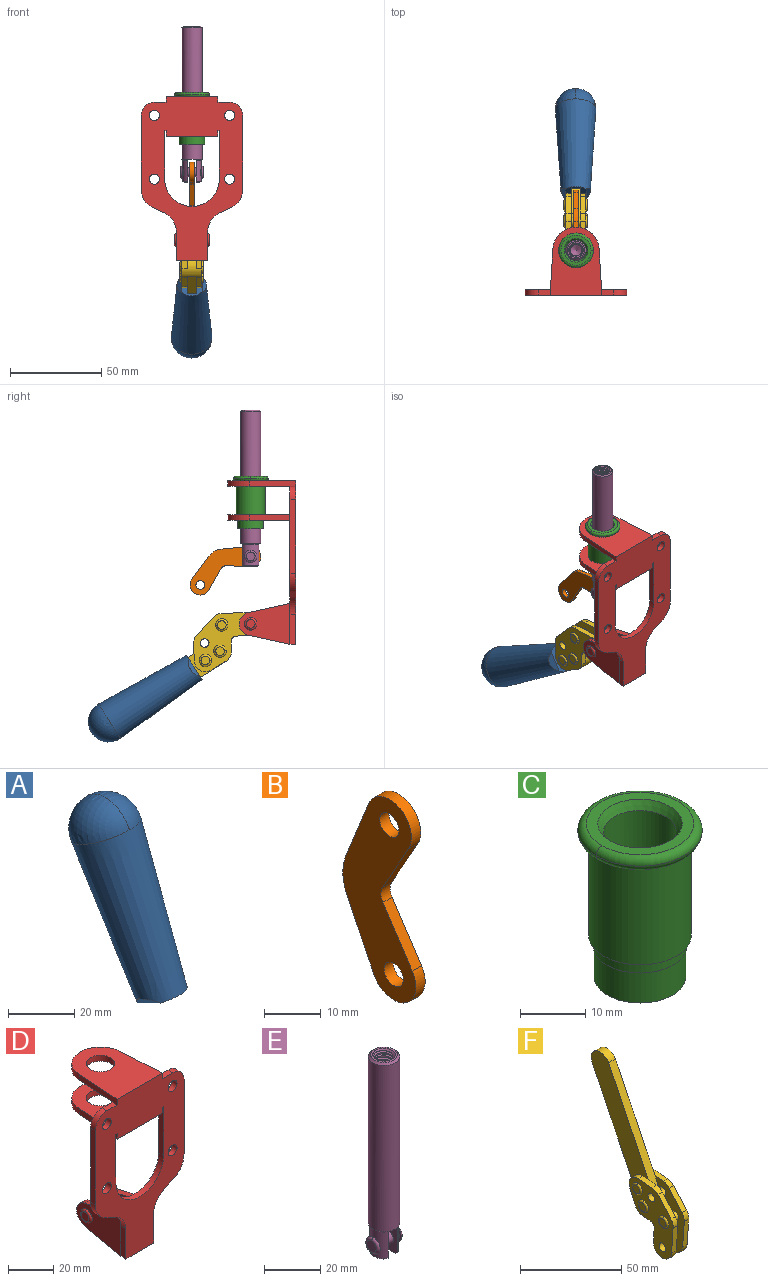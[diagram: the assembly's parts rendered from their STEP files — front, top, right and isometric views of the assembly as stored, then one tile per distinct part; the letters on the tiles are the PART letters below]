
ASSEMBLY  parts=6 mates=5
PART A: 11 faces, bbox 22.3x42.6x64.5 mm
  f0: sphere r=11.13mm, area 411.4mm2, adj f1,f8
  f1: cone r=11.11mm half-angle=3.3deg, axis (0,0.44,0.9), area 3251.8mm2, adj f0,f7,f8,f9,f10
  f2: cylinder r=6.16mm len=11.7mm, axis (1,0,0), area 89.5mm2, adj f3,f4,f5,f6
  f3: plane 60.23x36.75mm, normal (-1,0,0), area 763.6mm2, adj f2,f4,f6,f10
  f4: plane 51.37x25.05mm, normal (0,0.9,-0.44), area 264.2mm2, adj f2,f3,f5,f10
  f5: plane 60.23x36.75mm, normal (1,0,0), area 763.6mm2, adj f2,f4,f6,f10
  f6: plane 51.37x25.05mm, normal (0,-0.9,0.44), area 264.2mm2, adj f2,f3,f5,f10
  f7: plane 9.95x5.95mm, normal (0.71,-0.31,-0.64), area 25.8mm2, adj f1,f10
  f8: sphere r=11.13mm, area 411.4mm2, adj f0,f1
  f9: plane 9.95x5.95mm, normal (-0.71,-0.31,-0.64), area 25.8mm2, adj f1,f10
  f10: plane 14.27x11.38mm, normal (0,-0.44,-0.9), area 106.7mm2, adj f1,f3,f4,f5,f6,f7,f9
PART B: 12 faces, bbox 2.3x18.2x42.8 mm
  f0: cylinder r=2.4mm len=4.8mm, axis (1,0,0), area 34.9mm2, adj f4,f11
  f1: cylinder r=10.41mm len=8.47mm, axis (1,0,0), area 20.2mm2, adj f4,f9,f10,f11
  f2: cylinder r=3.05mm len=3.16mm, axis (1,0,0), area 7.7mm2, adj f4,f6,f7,f11
  f3: cylinder r=2.4mm len=4.8mm, axis (1,0,0), area 34.9mm2, adj f4,f11
  f4: plane 42.81x18.23mm, normal (-1,0,0), area 414.1mm2, adj f0,f1,f2,f3,f5,f6,f7,f8
  f5: cylinder r=5.54mm len=10.67mm, axis (1,0,0), area 41.8mm2, adj f4,f6,f10,f11
  f6: plane 11.66x6.53mm, normal (0,-0.87,-0.49), area 30.9mm2, adj f2,f4,f5,f11
  f7: plane 11.17x7.33mm, normal (0,-0.84,0.55), area 30.9mm2, adj f2,f4,f8,f11
  f8: cylinder r=5.54mm len=10.51mm, axis (1,0,0), area 41.8mm2, adj f4,f7,f9,f11
  f9: plane 13.67x6.67mm, normal (0,0.9,-0.44), area 35.1mm2, adj f1,f4,f8,f11
  f10: plane 14.1x5.7mm, normal (0,0.93,0.37), area 35.1mm2, adj f1,f4,f5,f11
  f11: plane 42.81x18.23mm, normal (1,0,0), area 414.1mm2, adj f0,f1,f2,f3,f5,f6,f7,f8
PART C: 15 faces, bbox 20.6x20.6x28.7 mm
  f0: torus R=8.26mm, axis (0,0,1), area 56.8mm2, adj f1,f10,f12
  f1: torus R=8.26mm, axis (0,0,1), area 56.8mm2, adj f0,f6,f13
  f2: cylinder r=5.59mm len=25.91mm, axis (0,0,1), area 909.6mm2, adj f3,f4
  f3: cone r=6.86mm half-angle=45deg, axis (0,0,-1), area 70.2mm2, adj f2,f14
  f4: cone r=6.47mm half-angle=30deg, axis (0,0,1), area 66.7mm2, adj f2,f13
  f5: cylinder r=7.04mm len=14.07mm, axis (0,0,1), area 252.6mm2, adj f11,f14
  f6: torus R=8.26mm, axis (0,0,1), area 56.8mm2, adj f1,f12,f13
  f7: cylinder r=7.16mm len=14.33mm, axis (0,0,1), area 91.5mm2, adj f9,f11
  f8: cylinder r=7.86mm len=18.42mm, axis (0,0,1), area 909.6mm2, adj f9,f10
  f9: plane 15.72x15.72mm, normal (0,0,-1), area 33mm2, adj f7,f8
  f10: plane 16.51x16.51mm, normal (0,0,-1), area 19.9mm2, adj f0,f8,f12
  f11: plane 14.33x14.33mm, normal (0,0,-1), area 5.7mm2, adj f5,f7
  f12: torus R=8.26mm, axis (0,0,1), area 56.8mm2, adj f0,f6,f10
  f13: plane 16.51x16.51mm, normal (0,0,1), area 82.7mm2, adj f1,f4,f6
  f14: plane 14.07x14.07mm, normal (0,0,-1), area 7.8mm2, adj f3,f5
PART D: 55 faces, bbox 55.7x37.4x89.8 mm
  f0: torus R=2.41mm, axis (-1,0,0), area 15mm2, adj f11,f15,f25
  f1: torus R=2.41mm, axis (-1,0,0), area 15mm2, adj f10,f12,f22
  f2: cylinder r=2.78mm len=5.56mm, axis (0,-1,0), area 54.2mm2, adj f30,f54
  f3: cylinder r=14.99mm len=29.97mm, axis (0,-1,0), area 145.9mm2, adj f30,f49,f53,f54
  f4: cylinder r=2.78mm len=5.56mm, axis (0,-1,0), area 54.2mm2, adj f30,f54
  f5: cylinder r=2.78mm len=5.56mm, axis (0,-1,0), area 54.2mm2, adj f30,f54
  f6: cylinder r=2.78mm len=5.56mm, axis (0,-1,0), area 54.2mm2, adj f30,f54
  f7: cylinder r=6.35mm len=12.7mm, axis (0,0,1), area 123.6mm2, adj f27,f51
  f8: cylinder r=6.35mm len=12.7mm, axis (0,0,-1), area 124.7mm2, adj f21,f35
  f9: cylinder r=2.41mm len=11.18mm, axis (-1,0,0), area 169.4mm2, adj f16,f19
  f10: plane 4.83x4.83mm, normal (1,0,0), area 18.3mm2, adj f1,f12
  f11: plane 4.83x4.83mm, normal (-1,0,0), area 18.3mm2, adj f0,f15
  f12: torus R=2.41mm, axis (-1,0,0), area 15mm2, adj f1,f10,f22
  f13: cylinder r=6.35mm len=12.41mm, axis (1,0,0), area 53.4mm2, adj f18,f19,f22,f23
  f14: cylinder r=6.35mm len=12.41mm, axis (-1,0,0), area 53.4mm2, adj f16,f17,f24,f25
  f15: torus R=2.41mm, axis (-1,0,0), area 15mm2, adj f0,f11,f25
  f16: plane 27.86x22.35mm, normal (1,0,0), area 425.4mm2, adj f9,f14,f17,f24,f30
  f17: plane 22.86x4.97mm, normal (0,0.21,0.98), area 72.5mm2, adj f14,f16,f25,f30
  f18: plane 22.86x4.97mm, normal (0,0.21,0.98), area 72.5mm2, adj f13,f19,f22,f30
  f19: plane 27.86x22.35mm, normal (-1,0,0), area 425.4mm2, adj f9,f13,f18,f23,f30
  f20: cylinder r=12.7mm len=25.35mm, axis (0,0,-1), area 119.8mm2, adj f21,f34,f35,f36
  f21: plane 34.21x28.07mm, normal (0,0,-1), area 702.4mm2, adj f8,f20,f30,f34,f36
  f22: plane 27.96x22.45mm, normal (1,0,0), area 407.2mm2, adj f1,f12,f13,f18,f23,f30,f42,f43
  f23: plane 22.86x4.97mm, normal (0,0.21,-0.98), area 72.5mm2, adj f13,f19,f22,f44
  f24: plane 22.86x4.97mm, normal (0,0.21,-0.98), area 72.5mm2, adj f14,f16,f25,f44
  f25: plane 27.86x22.35mm, normal (-1,0,0), area 407.1mm2, adj f0,f14,f15,f17,f24,f30,f45,f46
  f26: plane 3.1x0.95mm, normal (0,0,-1), area 2.7mm2, adj f30,f49,f50,f54
  f27: plane 34.21x28.07mm, normal (0,0,1), area 702.4mm2, adj f7,f28,f30,f50,f52
  f28: cylinder r=12.7mm len=25.35mm, axis (0,0,1), area 118.8mm2, adj f27,f50,f51,f52
  f29: plane 3.1x0.95mm, normal (0,0,-1), area 2.7mm2, adj f30,f52,f53,f54
  f30: plane 86.54x55.63mm, normal (0,1,0), area 2362.9mm2, adj f2,f3,f4,f5,f6,f16,f17,f18
  f31: plane 40.56x3.1mm, normal (-1,0,0), area 125.7mm2, adj f30,f32,f48,f54
  f32: cylinder r=7.11mm len=7.11mm, axis (0,-1,0), area 34.6mm2, adj f30,f31,f33,f54
  f33: plane 6.67x3.1mm, normal (0,0,1), area 20.4mm2, adj f30,f32,f34,f54
  f34: plane 25.39x3.13mm, normal (-1,0.06,0), area 79.5mm2, adj f20,f21,f33,f35,f54
  f35: plane 37.31x28.45mm, normal (0,0,1), area 789.9mm2, adj f8,f20,f34,f36,f54
  f36: plane 25.39x3.13mm, normal (1,0.06,0), area 79.5mm2, adj f20,f21,f35,f37,f54
  f37: plane 6.67x3.1mm, normal (0,0,1), area 20.4mm2, adj f30,f36,f38,f54
  f38: cylinder r=7.11mm len=7.11mm, axis (0,-1,0), area 34.6mm2, adj f30,f37,f39,f54
  f39: plane 40.56x3.1mm, normal (1,0,0), area 125.7mm2, adj f30,f38,f40,f54
  f40: cylinder r=11.18mm len=10.16mm, axis (0,-1,0), area 39.5mm2, adj f30,f39,f41,f54
  f41: plane 6.09x3.1mm, normal (0.42,0,-0.91), area 20.8mm2, adj f30,f40,f42,f54
  f42: cylinder r=11.18mm len=9.41mm, axis (0,-1,0), area 37.2mm2, adj f22,f30,f41,f43,f54
  f43: plane 16.5x3.1mm, normal (1,0,0), area 51.1mm2, adj f22,f42,f44,f54
  f44: plane 17.37x3.1mm, normal (0,0,-1), area 53.8mm2, adj f23,f24,f30,f43,f45,f54
  f45: plane 16.5x3.1mm, normal (-1,0,0), area 51.1mm2, adj f25,f44,f46,f54
  f46: cylinder r=11.18mm len=9.41mm, axis (0,-1,0), area 37.2mm2, adj f25,f30,f45,f47,f54
  f47: plane 6.09x3.1mm, normal (-0.42,0,-0.91), area 20.8mm2, adj f30,f46,f48,f54
  f48: cylinder r=11.18mm len=10.16mm, axis (0,-1,0), area 39.5mm2, adj f30,f31,f47,f54
  f49: plane 26.54x3.1mm, normal (-1,0,0), area 82.3mm2, adj f3,f26,f30,f54
  f50: plane 25.39x3.1mm, normal (1,0.06,0), area 78.8mm2, adj f26,f27,f28,f51,f54
  f51: plane 37.31x28.45mm, normal (0,0,-1), area 789.9mm2, adj f7,f28,f50,f52,f54
  f52: plane 25.39x3.1mm, normal (-1,0.06,0), area 78.8mm2, adj f27,f28,f29,f51,f54
  f53: plane 26.54x3.1mm, normal (1,0,0), area 82.3mm2, adj f3,f29,f30,f54
  f54: plane 89.66x55.63mm, normal (0,-1,0), area 2678.5mm2, adj f2,f3,f4,f5,f6,f26,f29,f31
PART E: 48 faces, bbox 12.6x11.1x86.1 mm
  f0: torus R=2.41mm, axis (-1,0,0), area 15mm2, adj f30,f32,f34
  f1: torus R=2.41mm, axis (-1,0,0), area 15mm2, adj f29,f31,f33
  f2: cylinder r=5.54mm len=72.39mm, axis (0,0,1), area 2518.5mm2, adj f3,f4,f42,f43
  f3: cone r=5.54mm half-angle=45deg, axis (0,0,1), area 7.6mm2, adj f2,f5,f41
  f4: cone r=5.54mm half-angle=45deg, axis (0,0,-1), area 34.9mm2, adj f2,f39
  f5: cylinder r=5.08mm len=11.48mm, axis (0,0,1), area 108.3mm2, adj f3,f7,f8,f41
  f6: cylinder r=2.41mm len=4.83mm, axis (-1,0,0), area 71.2mm2, adj f40,f41
  f7: cylinder r=2.41mm len=4.83mm, axis (-1,0,0), area 7.6mm2, adj f5,f34
  f8: cone r=5.08mm half-angle=45deg, axis (0,0,1), area 10.6mm2, adj f5,f37,f41
  f9: cone r=3.98mm half-angle=45deg, axis (0,0,1), area 17.6mm2, adj f27,f39,f45,f46,f47
  f10: cylinder r=2.41mm len=4.83mm, axis (-1,0,0), area 7.6mm2, adj f33,f38
  f11: cylinder r=3.2mm len=6.4mm, axis (0,0,1), area 78.4mm2, adj f12,f28,f44,f45,f47
  f12: cylinder r=3.2mm len=6.4mm, axis (0,0,1), area 10.5mm2, adj f11,f13,f45,f47
  f13: cylinder r=3.2mm len=6.4mm, axis (0,0,1), area 10.5mm2, adj f12,f14,f45,f47
  f14: cylinder r=3.2mm len=6.4mm, axis (0,0,1), area 10.5mm2, adj f13,f15,f45,f47
  f15: cylinder r=3.2mm len=6.4mm, axis (0,0,1), area 10.5mm2, adj f14,f16,f45,f47
  f16: cylinder r=3.2mm len=6.4mm, axis (0,0,1), area 10.5mm2, adj f15,f17,f45,f47
  f17: cylinder r=3.2mm len=6.4mm, axis (0,0,1), area 10.5mm2, adj f16,f18,f45,f47
  f18: cylinder r=3.2mm len=6.4mm, axis (0,0,1), area 10.5mm2, adj f17,f19,f45,f47
  f19: cylinder r=3.2mm len=6.4mm, axis (0,0,1), area 10.5mm2, adj f18,f20,f45,f47
  f20: cylinder r=3.2mm len=6.4mm, axis (0,0,1), area 10.5mm2, adj f19,f21,f45,f47
  f21: cylinder r=3.2mm len=6.4mm, axis (0,0,1), area 10.5mm2, adj f20,f22,f45,f47
  f22: cylinder r=3.2mm len=6.4mm, axis (0,0,1), area 10.5mm2, adj f21,f23,f45,f47
  f23: cylinder r=3.2mm len=6.4mm, axis (0,0,1), area 10.5mm2, adj f22,f24,f45,f47
  f24: cylinder r=3.2mm len=6.4mm, axis (0,0,1), area 10.5mm2, adj f23,f25,f45,f47
  f25: cylinder r=3.2mm len=6.4mm, axis (0,0,1), area 10.5mm2, adj f24,f26,f45,f47
  f26: cylinder r=3.2mm len=6.4mm, axis (0,0,1), area 10.5mm2, adj f25,f27,f45,f47
  f27: cylinder r=3.2mm len=6.4mm, axis (0,0,1), area 7.4mm2, adj f9,f26,f45,f47
  f28: cone r=3.2mm half-angle=60deg, axis (0,0,1), area 37.2mm2, adj f11
  f29: plane 4.83x4.83mm, normal (-1,0,0), area 18.3mm2, adj f1,f31
  f30: plane 4.83x4.83mm, normal (1,0,0), area 18.3mm2, adj f0,f32
  f31: torus R=2.41mm, axis (-1,0,0), area 15mm2, adj f1,f29,f33
  f32: torus R=2.41mm, axis (-1,0,0), area 15mm2, adj f0,f30,f34
  f33: plane 6.83x6.83mm, normal (1,0,0), area 18.3mm2, adj f1,f10,f31
  f34: plane 6.83x6.83mm, normal (-1,0,0), area 18.3mm2, adj f0,f7,f32
  f35: cone r=5.08mm half-angle=45deg, axis (0,0,1), area 10.6mm2, adj f36,f38,f40
  f36: plane 7.25x1.97mm, normal (0,0,-1), area 10mm2, adj f35,f40
  f37: plane 7.25x1.97mm, normal (0,0,-1), area 10mm2, adj f8,f41
  f38: cylinder r=5.08mm len=11.48mm, axis (0,0,1), area 108.3mm2, adj f10,f35,f40,f42
  f39: plane 9.55x9.55mm, normal (0,0,1), area 22mm2, adj f4,f9
  f40: plane 12.76x10.09mm, normal (1,0,0), area 95.7mm2, adj f6,f35,f36,f38,f42,f43
  f41: plane 12.76x10.09mm, normal (-1,0,0), area 95.7mm2, adj f3,f5,f6,f8,f37,f43
  f42: cone r=5.54mm half-angle=45deg, axis (0,0,1), area 7.6mm2, adj f2,f38,f40
  f43: plane 11.07x4.7mm, normal (0,0,-1), area 50.4mm2, adj f2,f40,f41
  f44: plane 0.89x0.62mm, normal (-1,0,0), area 0.3mm2, adj f11,f45,f46,f47
  f45: bspline ~24.8x7.63mm, area 266.6mm2, adj f9,f11,f12,f13,f14,f15,f16,f17
  f46: bspline ~24.87x7.63mm, area 73.6mm2, adj f9,f44,f45,f47
  f47: bspline ~24.98x7.63mm, area 272.5mm2, adj f9,f11,f12,f13,f14,f15,f16,f17
PART F: 59 faces, bbox 12.9x60.2x99.6 mm
  f0: torus R=2.39mm, axis (-1,0,0), area 14.9mm2, adj f20,f43,f51
  f1: torus R=2.39mm, axis (-1,0,0), area 14.9mm2, adj f19,f42,f51
  f2: torus R=2.39mm, axis (-1,0,0), area 14.9mm2, adj f18,f35,f51
  f3: torus R=2.39mm, axis (-1,0,0), area 14.9mm2, adj f14,f17,f23
  f4: torus R=2.39mm, axis (-1,0,0), area 14.9mm2, adj f13,f16,f23
  f5: torus R=2.39mm, axis (-1,0,0), area 14.9mm2, adj f12,f15,f23
  f6: cylinder r=2.39mm len=4.78mm, axis (1,0,0), area 46.5mm2, adj f48,f50,f51
  f7: cylinder r=2.39mm len=4.78mm, axis (1,0,0), area 46.5mm2, adj f50,f51
  f8: cylinder r=6.35mm len=12.68mm, axis (1,0,0), area 61.8mm2, adj f38,f39,f50,f51
  f9: cylinder r=2.39mm len=4.78mm, axis (-1,0,0), area 70.5mm2, adj f46,f50
  f10: cylinder r=2.39mm len=4.78mm, axis (-1,0,0), area 46.5mm2, adj f23,f45,f46
  f11: cylinder r=2.39mm len=4.78mm, axis (-1,0,0), area 46.5mm2, adj f23,f46
  f12: plane 4.78x4.78mm, normal (1,0,0), area 17.9mm2, adj f5,f15
  f13: plane 4.78x4.78mm, normal (1,0,0), area 17.9mm2, adj f4,f16
  f14: plane 4.78x4.78mm, normal (1,0,0), area 17.9mm2, adj f3,f17
  f15: torus R=2.39mm, axis (-1,0,0), area 14.9mm2, adj f5,f12,f23
  f16: torus R=2.39mm, axis (-1,0,0), area 14.9mm2, adj f4,f13,f23
  f17: torus R=2.39mm, axis (-1,0,0), area 14.9mm2, adj f3,f14,f23
  f18: plane 4.78x4.78mm, normal (-1,0,0), area 17.9mm2, adj f2,f35
  f19: plane 4.78x4.78mm, normal (-1,0,0), area 17.9mm2, adj f1,f42
  f20: plane 4.78x4.78mm, normal (-1,0,0), area 17.9mm2, adj f0,f43
  f21: plane 2.26x0.2mm, normal (1,0,0), area 0.2mm2, adj f31,f44
  f22: plane 2.26x0.2mm, normal (-1,0,0), area 0.2mm2, adj f41,f44
  f23: plane 39.37x30.77mm, normal (1,0,0), area 565.5mm2, adj f3,f4,f5,f10,f11,f15,f16,f17
  f24: cylinder r=6.1mm len=4.15mm, axis (-1,0,0), area 14.7mm2, adj f23,f25,f32,f46
  f25: plane 10.25x9.01mm, normal (0,-0.75,0.66), area 42.3mm2, adj f23,f24,f26,f46
  f26: cylinder r=6.35mm len=4.64mm, axis (-1,0,0), area 15.6mm2, adj f23,f25,f27,f46
  f27: plane 15.84x3.1mm, normal (0,-1,-0.07), area 49.2mm2, adj f23,f26,f28,f46
  f28: cylinder r=6.35mm len=12.68mm, axis (-1,0,0), area 61.8mm2, adj f23,f27,f29,f46
  f29: plane 8.11x3.1mm, normal (0,1,0.07), area 25.2mm2, adj f23,f28,f30,f46
  f30: cylinder r=3.05mm len=3.25mm, axis (-1,0,0), area 14.8mm2, adj f23,f29,f31,f46
  f31: plane 5.99x3.1mm, normal (0,0.07,-1), area 18.6mm2, adj f21,f23,f30,f44,f46
  f32: plane 9.5x3.1mm, normal (0,-0.07,1), area 29.5mm2, adj f23,f24,f33,f46,f47
  f33: cylinder r=6.1mm len=8.63mm, axis (-1,0,0), area 39.1mm2, adj f23,f32,f34,f47
  f34: plane 8.65x3.96mm, normal (0,0.91,-0.42), area 29.5mm2, adj f23,f33,f44,f47
  f35: torus R=2.39mm, axis (-1,0,0), area 14.9mm2, adj f2,f18,f51
  f36: plane 10.25x9.01mm, normal (0,-0.75,0.66), area 42.3mm2, adj f37,f49,f50,f51
  f37: cylinder r=6.35mm len=4.64mm, axis (1,0,0), area 15.6mm2, adj f36,f38,f50,f51
  f38: plane 15.84x3.1mm, normal (0,-1,-0.07), area 49.2mm2, adj f8,f37,f50,f51
  f39: plane 8.11x3.1mm, normal (0,1,0.07), area 25.2mm2, adj f8,f40,f50,f51
  f40: cylinder r=3.05mm len=3.25mm, axis (1,0,0), area 14.8mm2, adj f39,f41,f50,f51
  f41: plane 5.99x3.1mm, normal (0,0.07,-1), area 18.6mm2, adj f22,f40,f44,f50,f51
  f42: torus R=2.39mm, axis (-1,0,0), area 14.9mm2, adj f1,f19,f51
  f43: torus R=2.39mm, axis (-1,0,0), area 14.9mm2, adj f0,f20,f51
  f44: cylinder r=6.35mm len=12.12mm, axis (-1,0,0), area 128.9mm2, adj f21,f22,f23,f31,f34,f41,f46,f47
  f45: plane 2.65x1.35mm, normal (1,0,0), area 1mm2, adj f10,f55
  f46: plane 39.08x20.42mm, normal (-1,0,0), area 412.5mm2, adj f9,f10,f11,f24,f25,f26,f27,f28
  f47: plane 77.62x39.82mm, normal (1,0,0), area 850mm2, adj f32,f33,f34,f44,f53,f54,f55
  f48: plane 2.65x1.35mm, normal (-1,0,0), area 1mm2, adj f6,f55
  f49: cylinder r=6.1mm len=4.15mm, axis (1,0,0), area 14.7mm2, adj f36,f50,f51,f56
  f50: plane 39.08x20.42mm, normal (1,0,0), area 412.5mm2, adj f6,f7,f8,f9,f36,f37,f38,f39
  f51: plane 39.37x30.77mm, normal (-1,0,0), area 565.5mm2, adj f0,f1,f2,f6,f7,f8,f35,f36
  f52: plane 8.65x3.96mm, normal (0,0.91,-0.42), area 29.5mm2, adj f44,f51,f57,f58
  f53: plane 68.49x33.4mm, normal (0,0.9,-0.44), area 358.1mm2, adj f44,f47,f54,f58
  f54: cylinder r=6.35mm len=12.06mm, axis (1,0,0), area 93.7mm2, adj f47,f53,f55,f58
  f55: plane 68.49x33.4mm, normal (0,-0.9,0.44), area 358.1mm2, adj f44,f45,f46,f47,f48,f50,f54,f58
  f56: plane 9.5x3.1mm, normal (0,-0.07,1), area 29.5mm2, adj f49,f50,f51,f57,f58
  f57: cylinder r=6.1mm len=8.63mm, axis (1,0,0), area 39.1mm2, adj f51,f52,f56,f58
  f58: plane 77.62x39.82mm, normal (-1,0,0), area 850mm2, adj f44,f52,f53,f54,f55,f56,f57
PLACE A rot(axis=(-1,0,0),96.3deg) t=(-101.94,-4.6,20.3)mm
PLACE B rot(axis=(1,0,0),62.5deg) t=(-101.76,-34.87,6.17)mm
PLACE C t=(-101.76,-61.83,30.04)mm
PLACE D t=(-101.76,-61.83,30.25)mm fixed
PLACE E t=(-101.76,-61.83,19.67)mm
PLACE F rot(axis=(-1,0,0),96.3deg) t=(-101.9,-2.6,19.07)mm
MATE revolute B.f5 <-> E.f6  axis (1,0,0) through (-101.76,-37.22,35.15)mm
MATE fastened A.f5 <-> F.f58  axis (1,0,0) through (-104.25,19.91,-42.37)mm
MATE fastened C.f2 <-> D.f7  axis (0,0,1) through (-101.76,-37.22,58.02)mm
MATE slider E.f2 <-> C.f2  axis (0,0,1) through (-101.76,-37.22,78.45)mm
MATE revolute F.f7 <-> D.f0  axis (-1,0,0) through (-107.35,-37.22,-1.85)mm
